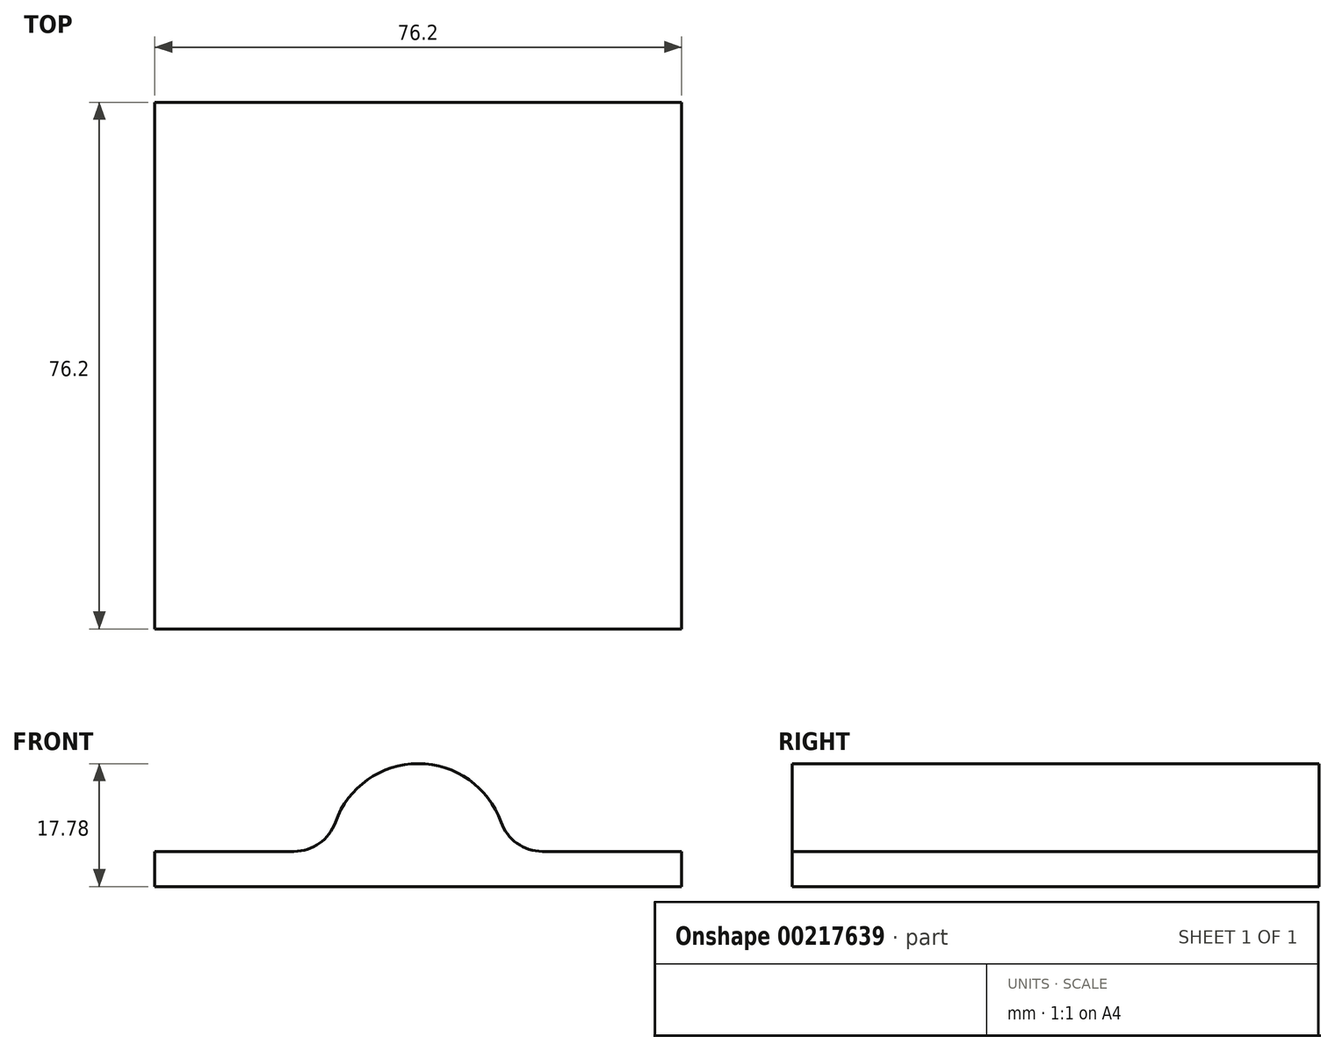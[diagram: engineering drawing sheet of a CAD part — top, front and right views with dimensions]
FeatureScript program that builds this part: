
annotation { "Feature Type Name" : "Feature", "Feature Type Description" : "" }
export const myFeature = defineFeature(function(context is Context, id is Id, definition is map)
    precondition{}
    {
        {
            var Q0;
            Q0=qCreatedBy(makeId("Front.planeOp"),FACE);
            var sketch = newSketch(context, id + "F0", { "sketchPlane" : qUnion([Q0])});
            skLineSegment(sketch, "E0.bottom", {"start": v(0, 0) * mm, "end": v(76.2, 0) * mm});
            skLineSegment(sketch, "E0.top", {"start": v(0, 76.2) * mm, "end": v(76.2, 76.2) * mm});
            skLineSegment(sketch, "E0.left", {"start": v(0, 0) * mm, "end": v(0, 76.2) * mm});
            skLineSegment(sketch, "E0.right", {"start": v(76.2, 0) * mm, "end": v(76.2, 76.2) * mm});
            skSolve(sketch);
        }
        {
            var Q0;
            Q0=makeQuery(id+"F0.imprint","IMPRINT",FACE,{"disambiguationData":[TD([[makeQuery(id+"F0.imprint","IMPRINT",EDGE,{"derivedFrom":sQuery(id+"F0.wireOp",EDGE,"E0.bottom")}),1.0]])]});
            extrude(context, id + "F1", {"entities" : qUnion([Q0]), "oppositeDirection" : true, "depth" : 5.08 * mm});
        }
        {
            var Q0;
            Q0=makeQuery(id+"F1.opExtrude","SWEPT_FACE",FACE,{"disambiguationData":[OSD([sQuery(id+"F0.wireOp",EDGE,"E0.bottom")])]});
            var sketch = newSketch(context, id + "F2", { "sketchPlane" : qUnion([Q0])});
            skArc(sketch, "E1", {"start": v(50.07, 4.23) * mm, "mid": v(38.1, 12.7) * mm, "end": v(26.13, 4.23) * mm});
            skLineSegment(sketch, "E2.0", {"start": v(0, 0) * mm, "end": v(20.14, 0) * mm});
            skLineSegment(sketch, "E3.0", {"start": v(0, -5.08) * mm, "end": v(76.2, -5.08) * mm});
            skPoint(sketch, "E4.newPointA", {"position": v(76.2, 0) * mm});
            skArc(sketch, "E4.filletArc", {"start": v(20.14, 0) * mm, "mid": v(23.8, 1.17) * mm, "end": v(26.13, 4.23) * mm});
            skLineSegment(sketch, "E5.0", {"start": v(56.06, 0) * mm, "end": v(76.2, 0) * mm});
            skArc(sketch, "E6.filletArc", {"start": v(50.07, 4.23) * mm, "mid": v(52.4, 1.17) * mm, "end": v(56.06, 0) * mm});
            skSolve(sketch);
        }
        {
            var Q0;
            Q0=makeQuery(id+"F2.imprint","IMPRINT",FACE,{"disambiguationData":[TD([[makeQuery(id+"F2.imprint","IMPRINT",EDGE,{"derivedFrom":sQuery(id+"F2.wireOp",EDGE,"E1")}),1.0]])]});
            extrude(context, id + "F3", {"entities" : qUnion([Q0]), "operationType" : NewBodyOperationType.ADD, "oppositeDirection" : true, "depth" : 76.2 * mm});
        }
        {
            var Q0;
            Q0=makeQuery(id+"F1.opExtrude","SWEPT_BODY",BODY,{"disambiguationData":[OSD([sQuery(id+"F0.wireOp",EDGE,"E0.bottom"),sQuery(id+"F0.wireOp",EDGE,"E0.top"),sQuery(id+"F0.wireOp",EDGE,"E0.left"),sQuery(id+"F0.wireOp",EDGE,"E0.right")])]});
            var Q1;
            {var subQ0=sQuery(id+"F0.wireOp",EDGE,"E0.left");var subQ2=sQuery(id+"F0.wireOp",EDGE,"E0.bottom");Q1=makeQuery(id+"F3.boolean.opBoolean","SPLIT",EDGE,{"disambiguationData":[TD([makeQuery(id+"F1.opExtrude","SWEPT_FACE",FACE,{"disambiguationData":[OSD([subQ0])]})])],"derivedFrom":makeQuery(id+"F1.opExtrude","CAP_EDGE",EDGE,{"disambiguationData":[OSD([subQ2])],"isStart":true})});}
            transform(context, id + "F4", {"entities" : qUnion([Q0]), "transformType" : TransformType.ROTATION, "transformAxis" : qUnion([Q1]), "angle" : 90 * degree, "oppositeDirection" : true, "makeCopy" : false});
        }
    });
